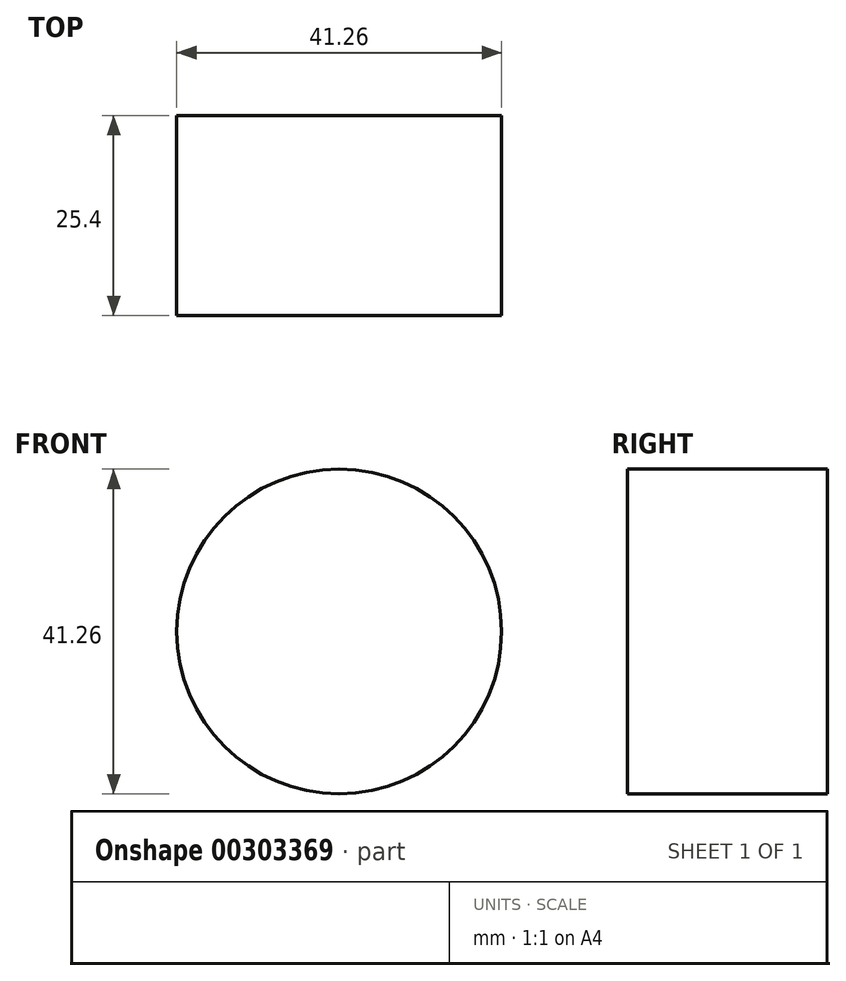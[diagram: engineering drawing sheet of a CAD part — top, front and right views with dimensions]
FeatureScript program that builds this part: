
annotation { "Feature Type Name" : "Feature", "Feature Type Description" : "" }
export const myFeature = defineFeature(function(context is Context, id is Id, definition is map)
    precondition{}
    {
        {
            var Q0;
            Q0=qCreatedBy(makeId("Front.planeOp"),FACE);
            var sketch = newSketch(context, id + "F0", { "sketchPlane" : qUnion([Q0])});
            skCircle(sketch, "E0", {"center": v(0, 0) * mm, "radius": 20.63 * mm});
            skSolve(sketch);
        }
        {
            var Q0;
            Q0=makeQuery(id+"F0.imprint","IMPRINT",FACE,{"disambiguationData":[TD([[makeQuery(id+"F0.imprint","IMPRINT",EDGE,{"derivedFrom":sQuery(id+"F0.wireOp",EDGE,"E0")}),1.0]])]});
            extrude(context, id + "F1", {"entities" : qUnion([Q0]), "depth" : 25.4 * mm});
        }
    });
